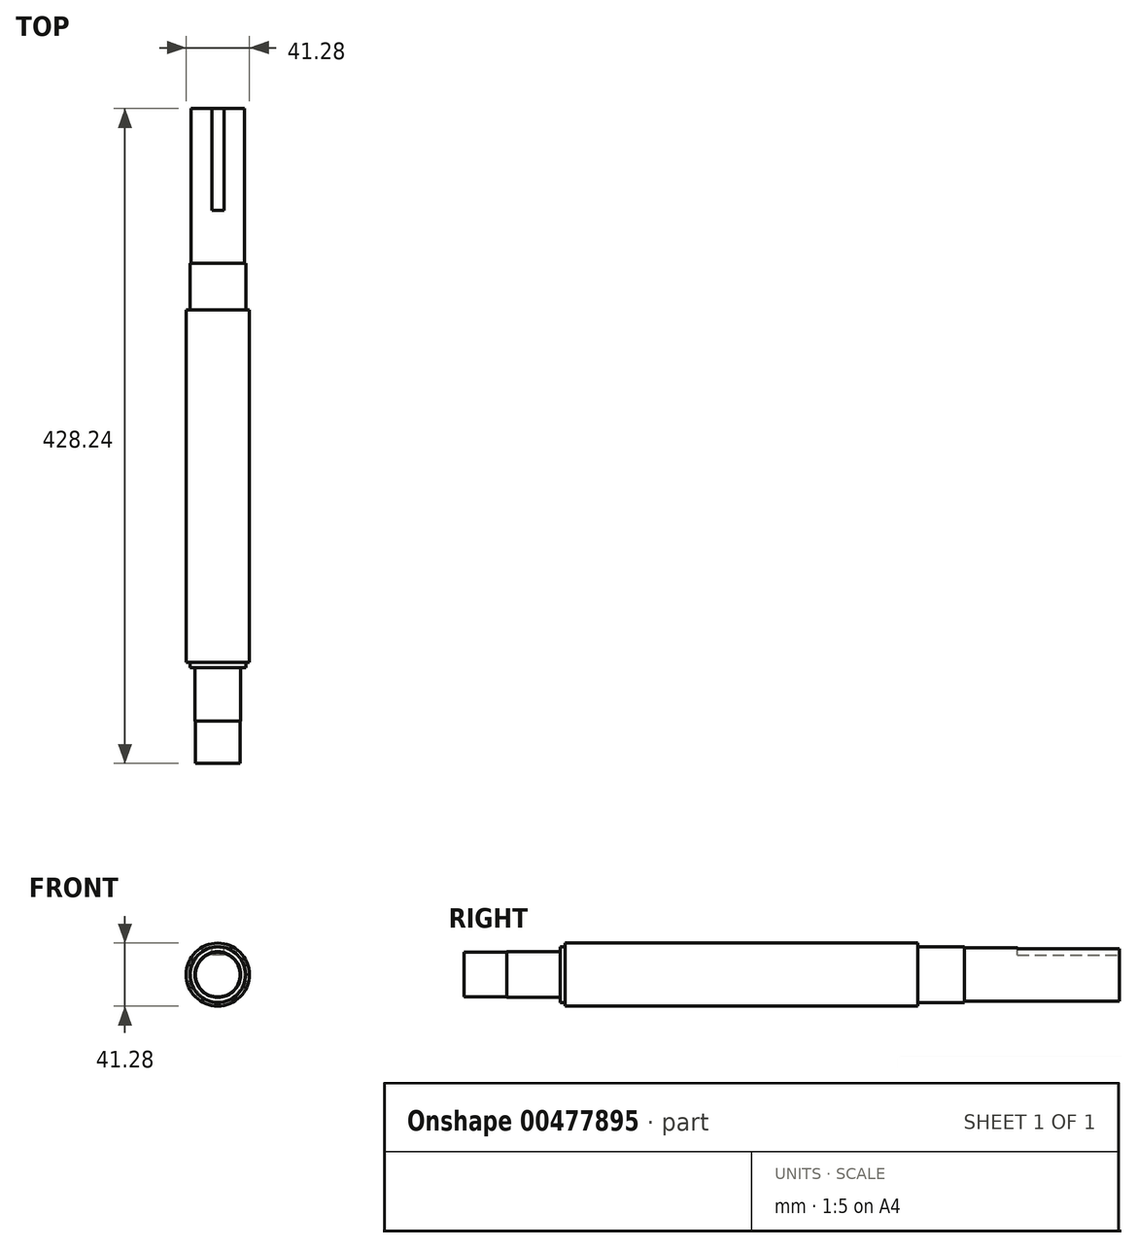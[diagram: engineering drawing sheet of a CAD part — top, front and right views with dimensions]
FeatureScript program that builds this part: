
annotation { "Feature Type Name" : "Feature", "Feature Type Description" : "" }
export const myFeature = defineFeature(function(context is Context, id is Id, definition is map)
    precondition{}
    {
        {
            var Q0;
            Q0=qCreatedBy(makeId("Right.planeOp"),FACE);
            var sketch = newSketch(context, id + "F0", { "sketchPlane" : qUnion([Q0])});
            skLineSegment(sketch, "E0", {"start": v(-135.1, 14.6) * mm, "end": v(-107.32, 14.6) * mm});
            skLineSegment(sketch, "E1", {"start": v(-107.32, 14.6) * mm, "end": v(-107.32, 14.96) * mm});
            skLineSegment(sketch, "E2", {"start": v(-107.32, 14.96) * mm, "end": v(-72.39, 14.96) * mm});
            skLineSegment(sketch, "E3", {"start": v(-72.4, 14.96) * mm, "end": v(-72.4, 18.26) * mm});
            skLineSegment(sketch, "E4", {"start": v(-72.4, 18.26) * mm, "end": v(-69.09, 18.26) * mm});
            skLineSegment(sketch, "E5", {"start": v(-69.09, 18.26) * mm, "end": v(-69.09, 20.64) * mm});
            skLineSegment(sketch, "E6", {"start": v(-69.09, 20.64) * mm, "end": v(161.6, 20.64) * mm});
            skLineSegment(sketch, "E7", {"start": v(161.6, 20.64) * mm, "end": v(161.6, 18.26) * mm});
            skLineSegment(sketch, "E8", {"start": v(161.6, 18.26) * mm, "end": v(192.05, 18.26) * mm});
            skLineSegment(sketch, "E9", {"start": v(192.05, 18.26) * mm, "end": v(192.05, 17.46) * mm});
            skLineSegment(sketch, "E10", {"start": v(192.05, 17.46) * mm, "end": v(293.14, 17.46) * mm});
            skLineSegment(sketch, "E11", {"start": v(293.14, 17.46) * mm, "end": v(293.14, 0) * mm});
            skLineSegment(sketch, "E12", {"start": v(293.14, 0) * mm, "end": v(0, 0) * mm});
            skLineSegment(sketch, "E13", {"start": v(-135.1, 14.6) * mm, "end": v(-135.1, 0) * mm});
            skLineSegment(sketch, "E14", {"start": v(-135.1, 0) * mm, "end": v(0, 0) * mm});
            skSolve(sketch);
        }
        {
            var Q0;
            Q0=makeQuery(id+"F0.imprint","IMPRINT",FACE,{"disambiguationData":[TD([[makeQuery(id+"F0.imprint","IMPRINT",EDGE,{"derivedFrom":sQuery(id+"F0.wireOp",EDGE,"jf98gD07-Kvmx-RvMU-AE7r-MhDOoLDJlLie")}),-1.0]])]});
            var Q1;
            Q1=makeQuery(id+"F0.imprint","IMPRINT",FACE,{"disambiguationData":[TD([[makeQuery(id+"F0.imprint","IMPRINT",EDGE,{"derivedFrom":sQuery(id+"F0.wireOp",EDGE,"E0")}),-1.0]])]});
            var Q2;
            Q2=sQuery(id+"F0.wireOp",EDGE,"E12");
            revolve(context, id + "F1", {"entities" : qUnion([Q0, Q1]), "axis" : qUnion([Q2]), "revolveType" : RevolveType.FULL});
        }
        {
            var Q0;
            Q0=makeQuery(id+"F1.opRevolve","SWEPT_FACE",FACE,{"disambiguationData":[OSD([sQuery(id+"F0.wireOp",EDGE,"E11")])]});
            var sketch = newSketch(context, id + "F2", { "sketchPlane" : qUnion([Q0])});
            skLineSegment(sketch, "E15", {"start": v(-3.97, 12.84) * mm, "end": v(3.97, 12.84) * mm});
            skLineSegment(sketch, "E16", {"start": v(3.97, 12.84) * mm, "end": v(3.97, 30.2) * mm});
            skLineSegment(sketch, "E17", {"start": v(3.97, 30.2) * mm, "end": v(-3.97, 30.2) * mm});
            skLineSegment(sketch, "E18", {"start": v(-3.97, 12.84) * mm, "end": v(-3.97, 30.2) * mm});
            skSolve(sketch);
        }
        {
            var Q0;
            {var subQ0=sQuery(id+"F2.wireOp",EDGE,"E15");Q0=makeQuery(id+"F2.imprint","IMPRINT",FACE,{"disambiguationData":[TD([[makeQuery(id+"F2.imprint","IMPRINT",EDGE,{"derivedFrom":subQ0}),1.0]])]});}
            extrude(context, id + "F3", {"entities" : qUnion([Q0]), "operationType" : NewBodyOperationType.REMOVE, "oppositeDirection" : true, "depth" : 66.55 * mm});
        }
    });
